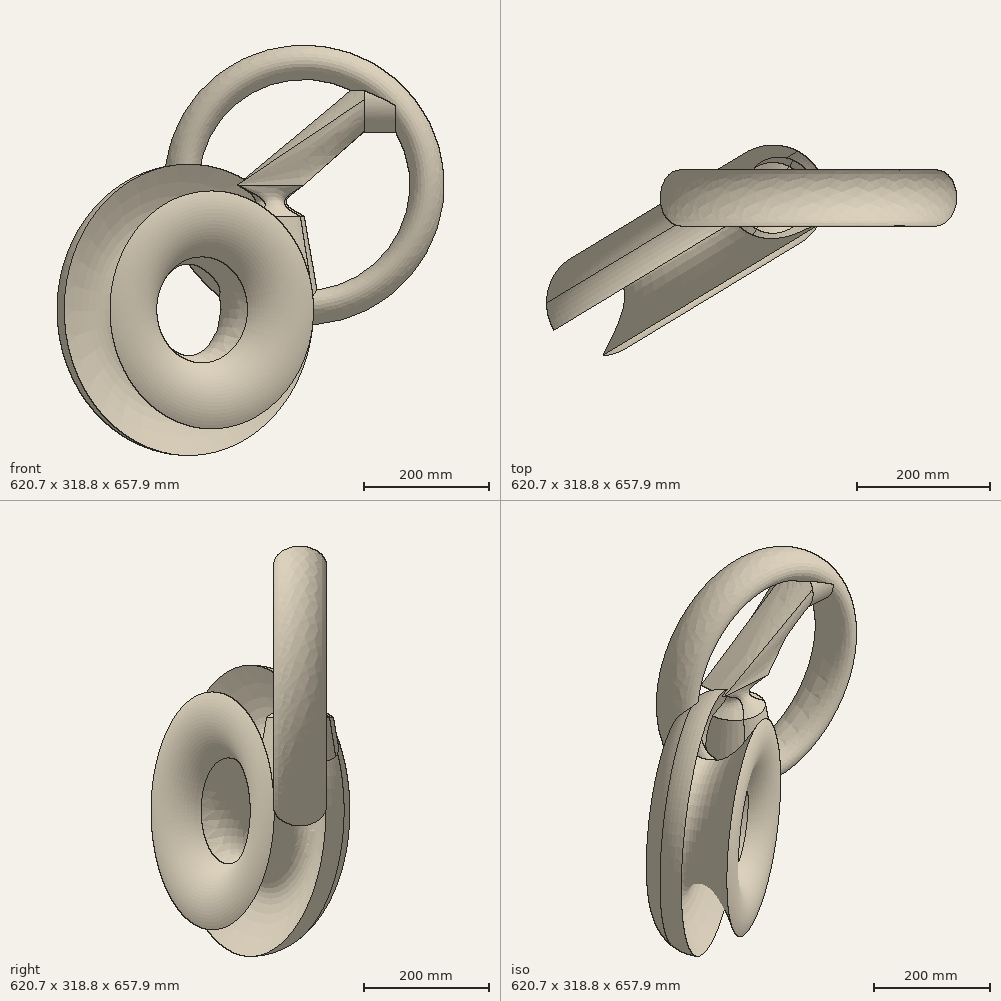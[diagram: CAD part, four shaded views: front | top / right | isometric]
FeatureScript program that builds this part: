
annotation { "Feature Type Name" : "Feature", "Feature Type Description" : "" }
export const myFeature = defineFeature(function(context is Context, id is Id, definition is map)
    precondition{}
    {
        {
            var Q0;
            Q0=qCreatedBy(makeId("Top.planeOp"),FACE);
            cPlane(context, id + "F0", {"entities" : qUnion([Q0]), "cplaneType" : CPlaneType.OFFSET, "offset" : 25 * mm, "width" : 150 * mm, "height" : 150 * mm});
        }
        {
            var Q0;
            Q0=qCreatedBy(makeId("Top.planeOp"),FACE);
            var sketch = newSketch(context, id + "F1", { "sketchPlane" : qUnion([Q0])});
            skCircle(sketch, "E0", {"center": v(0, 0) * mm, "radius": 53.49 * mm});
            skSolve(sketch);
        }
        {
            var Q0;
            Q0=qCreatedBy(id+"F0.planeOp",FACE);
            var sketch = newSketch(context, id + "F2", { "sketchPlane" : qUnion([Q0])});
            skCircle(sketch, "E1", {"center": v(0, 0) * mm, "radius": 25.36 * mm});
            skSolve(sketch);
        }
        {
            var Q0;
            Q0=qCreatedBy(id+"F0.planeOp",FACE);
            cPlane(context, id + "F3", {"entities" : qUnion([Q0]), "cplaneType" : CPlaneType.OFFSET, "offset" : 25 * mm, "width" : 150 * mm, "height" : 150 * mm});
        }
        {
            var Q0;
            Q0=qCreatedBy(id+"F3.planeOp",FACE);
            var sketch = newSketch(context, id + "F4", { "sketchPlane" : qUnion([Q0])});
            skLineSegment(sketch, "E2.bottom", {"start": v(53.48, -28.4) * mm, "end": v(-53.48, -28.4) * mm});
            skLineSegment(sketch, "E2.top", {"start": v(53.48, 28.4) * mm, "end": v(-53.48, 28.4) * mm});
            skLineSegment(sketch, "E2.left", {"start": v(53.48, -28.4) * mm, "end": v(53.48, 28.4) * mm});
            skLineSegment(sketch, "E2.right", {"start": v(-53.48, -28.4) * mm, "end": v(-53.48, 28.4) * mm});
            skPoint(sketch, "E2.middle", {"position": v(0, 0) * mm});
            skSolve(sketch);
        }
        {
            var Q0;
            Q0=makeQuery(id+"F4.imprint","IMPRINT",FACE,{"disambiguationData":[TD([[makeQuery(id+"F4.imprint","IMPRINT",EDGE,{"derivedFrom":sQuery(id+"F4.wireOp",EDGE,"E2.bottom")}),-1.0]])]});
            var Q1;
            Q1=makeQuery(id+"F2.imprint","IMPRINT",FACE,{"disambiguationData":[TD([[makeQuery(id+"F2.imprint","IMPRINT",EDGE,{"derivedFrom":sQuery(id+"F2.wireOp",EDGE,"E1")}),1.0]])]});
            var Q2;
            Q2 = qSketchRegion(id + "F1", true);
            loft(context, id + "F5", {"sheetProfilesArray" : [{ "sheetProfileEntities" : qUnion([Q0]) }, { "sheetProfileEntities" : qUnion([Q1]) }, { "sheetProfileEntities" : qUnion([Q2]) }]});
        }
        {
            var Q0;
            Q0=qCreatedBy(makeId("Right.planeOp"),FACE);
            cPlane(context, id + "F6", {"entities" : qUnion([Q0]), "cplaneType" : CPlaneType.OFFSET, "offset" : 150 * mm, "width" : 150 * mm, "height" : 150 * mm});
        }
        {
            var Q0;
            Q0=qCreatedBy(id+"F6.planeOp",FACE);
            var sketch = newSketch(context, id + "F7", { "sketchPlane" : qUnion([Q0])});
            skCircle(sketch, "E3", {"center": v(0, 177.45) * mm, "radius": 42.47 * mm});
            skSolve(sketch);
        }
        {
            var Q1;
            Q1 = qSketchRegion(id + "F7", true);
            var Q2;
            Q2=makeQuery(id+"F5.opLoft","CAP_FACE",FACE,{"disambiguationData":[OSD([makeQuery(id+"F4.imprint","IMPRINT",FACE,{"disambiguationData":[TD([[makeQuery(id+"F4.imprint","IMPRINT",EDGE,{"derivedFrom":sQuery(id+"F4.wireOp",EDGE,"E2.bottom")}),-1.0]])]})])],"isStart":true});
            loft(context, id + "F8", {"operationType" : NewBodyOperationType.ADD, "sheetProfilesArray" : [{ "sheetProfileEntities" : qUnion([Q1]) }, { "sheetProfileEntities" : qUnion([Q2]) }]});
        }
        {
            var Q0;
            Q0=makeQuery(id+"F7.imprint","IMPRINT",FACE,{"disambiguationData":[TD([[makeQuery(id+"F7.imprint","IMPRINT",EDGE,{"derivedFrom":sQuery(id+"F7.wireOp",EDGE,"E3")}),1.0]])]});
            extrude(context, id + "F9", {"entities" : qUnion([Q0]), "operationType" : NewBodyOperationType.ADD, "depth" : 50 * mm, "offsetDistance" : 25 * mm});
        }
        {
            var Q0;
            Q0=makeQuery(id+"F9.opExtrude","CAP_FACE",FACE,{"disambiguationData":[OSD([sQuery(id+"F7.wireOp",EDGE,"E3")])],"isStart":false});
            var Q1;
            {var subQ0=sQuery(id+"F4.wireOp",EDGE,"E2.left");var subQ1=sQuery(id+"F4.wireOp",EDGE,"E2.top");var subQ2=sQuery(id+"F4.wireOp",EDGE,"E2.bottom");Q1=makeQuery(id+"F8.boolean.opBoolean","MERGE",EDGE,{"derivedFrom":[makeQuery(id+"F5.opLoft","MID_CAP_EDGE",EDGE,{"disambiguationData":[OSD([subQ2,subQ1,subQ0])],"capPos":0.0}),makeQuery(id+"F8.opLoft","MID_CAP_EDGE",EDGE,{"disambiguationData":[OSD([subQ2,subQ1,subQ0])],"capPos":1.0})]});}
            revolve(context, id + "F10", {"operationType" : NewBodyOperationType.ADD, "entities" : qUnion([Q0]), "axis" : qUnion([Q1]), "revolveType" : RevolveType.FULL});
        }
        {
            var Q0;
            Q0=makeQuery(id+"F5.opLoft","CAP_FACE",FACE,{"disambiguationData":[OSD([makeQuery(id+"F1.imprint","IMPRINT",FACE,{"disambiguationData":[TD([[makeQuery(id+"F1.imprint","IMPRINT",EDGE,{"derivedFrom":sQuery(id+"F1.wireOp",EDGE,"E0")}),1.0]])]})])],"isStart":true});
            extrude(context, id + "F11", {"entities" : qUnion([Q0]), "operationType" : NewBodyOperationType.ADD, "depth" : 150 * mm, "offsetDistance" : 25 * mm, "hasDraft" : true, "draftAngle" : 10 * degree});
        }
        {
            var Q0;
            Q0=makeQuery(id+"F11.opExtrude","CAP_FACE",FACE,{"disambiguationData":[OSD([makeQuery(id+"F1.imprint","IMPRINT",FACE,{"disambiguationData":[TD([[makeQuery(id+"F1.imprint","IMPRINT",EDGE,{"derivedFrom":sQuery(id+"F1.wireOp",EDGE,"E0")}),1.0]])]})])],"isStart":false});
            var sketch = newSketch(context, id + "F12", { "sketchPlane" : qUnion([Q0])});
            skLineSegment(sketch, "E4", {"start": v(-114.96, 106.78) * mm, "end": v(-206.72, -44.88) * mm});
            skSolve(sketch);
        }
        {
            var Q0;
            {var subQ4=sQuery(id+"F1.wireOp",EDGE,"E0");Q0=makeQuery(id+"F12.imprint","IMPRINT",FACE,{"disambiguationData":[TD([[makeQuery(id+"F12.imprint","IMPRINT",EDGE,{"derivedFrom":makeQuery(id+"F11.boolean.opBoolean","INTERSECT",EDGE,{"derivedFrom":[makeQuery(id+"F10.opRevolve","SWEPT_FACE",FACE,{"disambiguationData":[OSD([sQuery(id+"F7.wireOp",EDGE,"E3")])]}),makeQuery(id+"F11.opExtrude","CAP_FACE",FACE,{"disambiguationData":[OSD([makeQuery(id+"F1.imprint","IMPRINT",FACE,{"disambiguationData":[TD([[makeQuery(id+"F1.imprint","IMPRINT",EDGE,{"derivedFrom":subQ4}),1.0]])]})])],"isStart":false})]})}),1.0]])]});}
            var Q1;
            Q1=sQuery(id+"F12.wireOp",EDGE,"E4");
            revolve(context, id + "F13", {"operationType" : NewBodyOperationType.ADD, "entities" : qUnion([Q0]), "axis" : qUnion([Q1]), "revolveType" : RevolveType.FULL});
        }
    });
